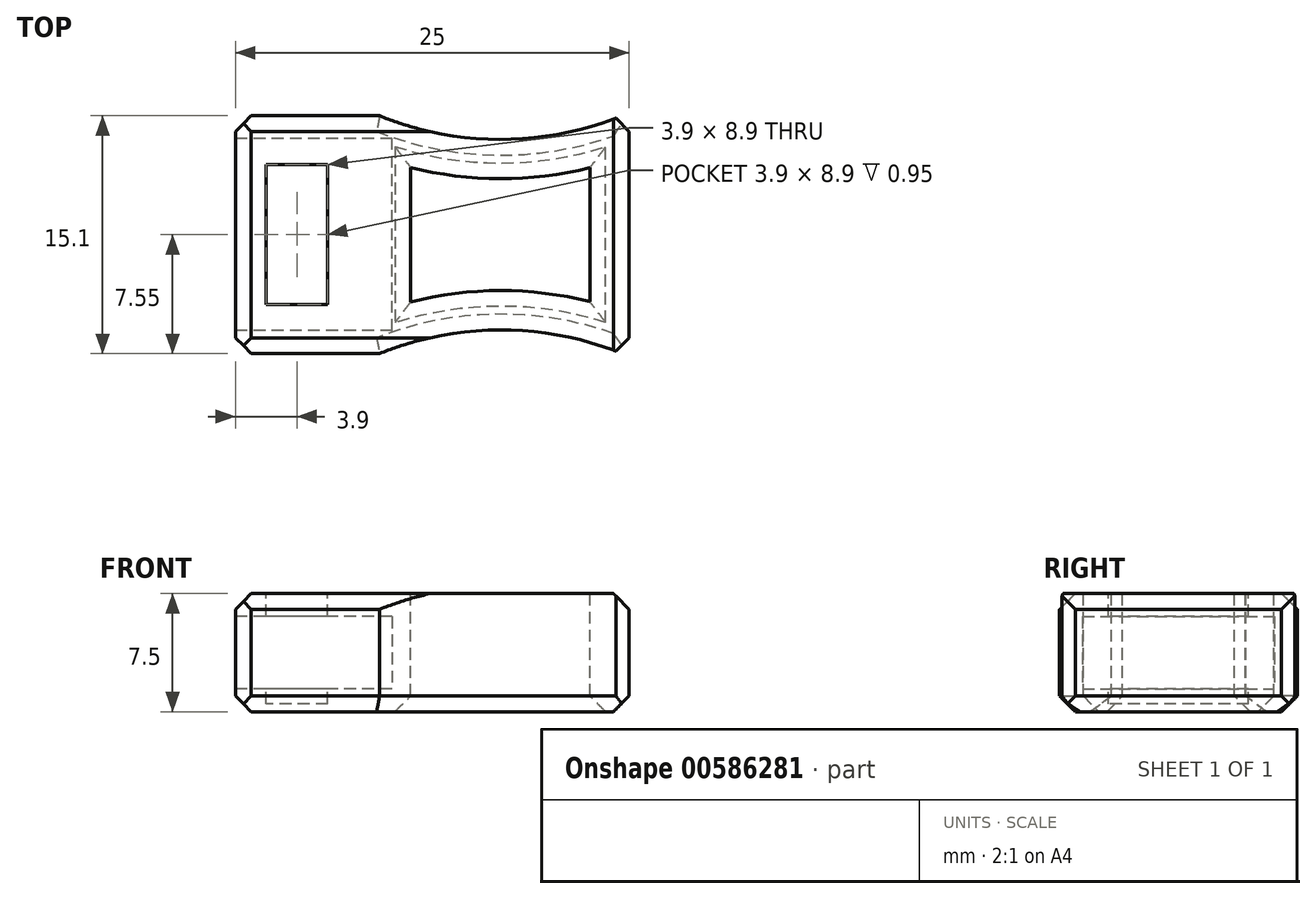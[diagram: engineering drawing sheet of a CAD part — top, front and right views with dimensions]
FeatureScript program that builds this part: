
annotation { "Feature Type Name" : "Feature", "Feature Type Description" : "" }
export const myFeature = defineFeature(function(context is Context, id is Id, definition is map)
    precondition{}
    {
        {
            var Q0;
            Q0=qCreatedBy(makeId("Top.planeOp"),FACE);
            var sketch = newSketch(context, id + "F0", { "sketchPlane" : qUnion([Q0])});
            skLineSegment(sketch, "E0.bottom", {"start": v(25, 7.55) * mm, "end": v(0, 7.55) * mm});
            skLineSegment(sketch, "E0.top", {"start": v(25, -7.55) * mm, "end": v(0, -7.55) * mm});
            skLineSegment(sketch, "E0.left", {"start": v(25, 7.55) * mm, "end": v(25, -7.55) * mm});
            skLineSegment(sketch, "E0.right", {"start": v(0, 7.55) * mm, "end": v(0, -7.55) * mm});
            skPoint(sketch, "E0.middle", {"position": v(0, 0) * mm});
            skSolve(sketch);
        }
        {
            var Q0;
            Q0 = qSketchRegion(id + "F0", true);
            extrude(context, id + "F1", {"entities" : qUnion([Q0]), "depth" : 7.5 * mm, "offsetDistance" : 25 * mm});
        }
        {
            var Q0;
            Q0=makeQuery(id+"F1.opExtrude","SWEPT_FACE",FACE,{"disambiguationData":[OSD([sQuery(id+"F0.wireOp",EDGE,"E0.right")])]});
            var sketch = newSketch(context, id + "F2", { "sketchPlane" : qUnion([Q0])});
            skLineSegment(sketch, "E1.bottom", {"start": v(6.1, 6.05) * mm, "end": v(-6.1, 6.05) * mm});
            skLineSegment(sketch, "E1.top", {"start": v(6.1, 1.45) * mm, "end": v(-6.1, 1.45) * mm});
            skLineSegment(sketch, "E1.left", {"start": v(6.1, 6.05) * mm, "end": v(6.1, 1.45) * mm});
            skLineSegment(sketch, "E1.right", {"start": v(-6.1, 6.05) * mm, "end": v(-6.1, 1.45) * mm});
            skPoint(sketch, "E1.middle", {"position": v(0, 3.75) * mm});
            skSolve(sketch);
        }
        {
            var Q0;
            Q0 = qSketchRegion(id + "F2", true);
            extrude(context, id + "F3", {"entities" : qUnion([Q0]), "operationType" : NewBodyOperationType.REMOVE, "oppositeDirection" : true, "depth" : 9.95 * mm, "offsetDistance" : 25 * mm});
        }
        {
            var Q0;
            Q0=makeQuery(id+"F1.opExtrude","CAP_FACE",FACE,{"disambiguationData":[OSD([sQuery(id+"F0.wireOp",EDGE,"E0.bottom"),sQuery(id+"F0.wireOp",EDGE,"E0.top"),sQuery(id+"F0.wireOp",EDGE,"E0.left"),sQuery(id+"F0.wireOp",EDGE,"E0.right")])],"isStart":false});
            var sketch = newSketch(context, id + "F4", { "sketchPlane" : qUnion([Q0])});
            skLineSegment(sketch, "E2.bottom", {"start": v(5.85, 4.45) * mm, "end": v(1.95, 4.45) * mm});
            skLineSegment(sketch, "E2.top", {"start": v(5.85, -4.45) * mm, "end": v(1.95, -4.45) * mm});
            skLineSegment(sketch, "E2.left", {"start": v(5.85, 4.45) * mm, "end": v(5.85, -4.45) * mm});
            skLineSegment(sketch, "E2.right", {"start": v(1.95, 4.45) * mm, "end": v(1.95, -4.45) * mm});
            skPoint(sketch, "E2.middle", {"position": v(3.9, 0) * mm});
            skSolve(sketch);
        }
        {
            var Q0;
            Q0 = qSketchRegion(id + "F4", true);
            extrude(context, id + "F5", {"entities" : qUnion([Q0]), "operationType" : NewBodyOperationType.REMOVE, "oppositeDirection" : true, "depth" : 25 * mm, "offsetDistance" : 25 * mm});
        }
        {
            var Q0;
            Q0=makeQuery(id+"F1.opExtrude","SWEPT_FACE",FACE,{"disambiguationData":[OSD([sQuery(id+"F0.wireOp",EDGE,"E0.left")])]});
            chamfer(context, id + "F6", {"entities" : qUnion([Q0]), "width" : 1 * mm, "tangentPropagation" : true});
        }
        {
            var Q0;
            Q0=makeQuery(id+"F1.opExtrude","CAP_EDGE",EDGE,{"disambiguationData":[OSD([sQuery(id+"F0.wireOp",EDGE,"E0.right")])],"isStart":false});
            var Q1;
            Q1=makeQuery(id+"F1.opExtrude","SWEPT_EDGE",EDGE,{"disambiguationData":[OSD([sQuery(id+"F0.wireOp",EDGE,"E0.top"),sQuery(id+"F0.wireOp",EDGE,"E0.right")])]});
            var Q2;
            Q2=makeQuery(id+"FrfRJ4BR4iio1pi_1.opChamfer","BLEND_EDGE",EDGE,{"blendedFrom":[makeQuery(id+"F1.opExtrude","CAP_EDGE",EDGE,{"disambiguationData":[OSD([sQuery(id+"F0.wireOp",EDGE,"E0.top")])],"isStart":false}),makeQuery(id+"F1.opExtrude","SWEPT_FACE",FACE,{"disambiguationData":[OSD([sQuery(id+"F0.wireOp",EDGE,"E0.right")])]})],"blendedInto":[makeQuery(id+"F1.opExtrude","SWEPT_FACE",FACE,{"disambiguationData":[OSD([sQuery(id+"F0.wireOp",EDGE,"E0.right")])]})]});
            var Q3;
            Q3=makeQuery(id+"FrfRJ4BR4iio1pi_1.opChamfer","BLEND_EDGE",EDGE,{"blendedFrom":[makeQuery(id+"F1.opExtrude","CAP_EDGE",EDGE,{"disambiguationData":[OSD([sQuery(id+"F0.wireOp",EDGE,"E0.top")])],"isStart":true}),makeQuery(id+"F1.opExtrude","SWEPT_FACE",FACE,{"disambiguationData":[OSD([sQuery(id+"F0.wireOp",EDGE,"E0.right")])]})],"blendedInto":[makeQuery(id+"F1.opExtrude","SWEPT_FACE",FACE,{"disambiguationData":[OSD([sQuery(id+"F0.wireOp",EDGE,"E0.right")])]})]});
            var Q4;
            Q4=makeQuery(id+"F1.opExtrude","CAP_EDGE",EDGE,{"disambiguationData":[OSD([sQuery(id+"F0.wireOp",EDGE,"E0.right")])],"isStart":true});
            var Q5;
            Q5=makeQuery(id+"FrfRJ4BR4iio1pi_1.opChamfer","BLEND_EDGE",EDGE,{"blendedFrom":[makeQuery(id+"F1.opExtrude","CAP_EDGE",EDGE,{"disambiguationData":[OSD([sQuery(id+"F0.wireOp",EDGE,"E0.bottom")])],"isStart":false}),makeQuery(id+"F1.opExtrude","SWEPT_FACE",FACE,{"disambiguationData":[OSD([sQuery(id+"F0.wireOp",EDGE,"E0.right")])]})],"blendedInto":[makeQuery(id+"F1.opExtrude","SWEPT_FACE",FACE,{"disambiguationData":[OSD([sQuery(id+"F0.wireOp",EDGE,"E0.right")])]})]});
            var Q6;
            Q6=makeQuery(id+"F1.opExtrude","SWEPT_EDGE",EDGE,{"disambiguationData":[OSD([sQuery(id+"F0.wireOp",EDGE,"E0.bottom"),sQuery(id+"F0.wireOp",EDGE,"E0.right")])]});
            var Q7;
            Q7=makeQuery(id+"FrfRJ4BR4iio1pi_1.opChamfer","BLEND_EDGE",EDGE,{"blendedFrom":[makeQuery(id+"F1.opExtrude","CAP_EDGE",EDGE,{"disambiguationData":[OSD([sQuery(id+"F0.wireOp",EDGE,"E0.bottom")])],"isStart":true}),makeQuery(id+"F1.opExtrude","SWEPT_FACE",FACE,{"disambiguationData":[OSD([sQuery(id+"F0.wireOp",EDGE,"E0.right")])]})],"blendedInto":[makeQuery(id+"F1.opExtrude","SWEPT_FACE",FACE,{"disambiguationData":[OSD([sQuery(id+"F0.wireOp",EDGE,"E0.right")])]})]});
            chamfer(context, id + "F7", {"entities" : qUnion([Q0, Q1, Q2, Q3, Q4, Q5, Q6, Q7]), "width" : 1 * mm, "tangentPropagation" : true});
        }
        {
            var Q0;
            Q0=makeQuery(id+"F1.opExtrude","CAP_FACE",FACE,{"disambiguationData":[OSD([sQuery(id+"F0.wireOp",EDGE,"E0.bottom"),sQuery(id+"F0.wireOp",EDGE,"E0.top"),sQuery(id+"F0.wireOp",EDGE,"E0.left"),sQuery(id+"F0.wireOp",EDGE,"E0.right")])],"isStart":false});
            var sketch = newSketch(context, id + "F8", { "sketchPlane" : qUnion([Q0])});
            skCircle(sketch, "E3", {"center": v(16.85, 26.55) * mm, "radius": 20.5 * mm});
            skCircle(sketch, "E4", {"center": v(16.85, -26.55) * mm, "radius": 20.5 * mm});
            skSolve(sketch);
        }
        {
            var Q0;
            Q0 = qSketchRegion(id + "F8", true);
            extrude(context, id + "F9", {"entities" : qUnion([Q0]), "operationType" : NewBodyOperationType.REMOVE, "oppositeDirection" : true, "depth" : 25 * mm, "offsetDistance" : 25 * mm});
        }
        {
            var Q0;
            Q0=makeQuery(id+"F9.boolean.opBoolean","COPY",EDGE,{"derivedFrom":makeQuery(id+"F9.opExtrude","CAP_EDGE",EDGE,{"disambiguationData":[OSD([sQuery(id+"F8.wireOp",EDGE,"E4")])],"isStart":true})});
            var Q1;
            Q1=makeQuery(id+"F1.opExtrude","CAP_EDGE",EDGE,{"disambiguationData":[OSD([sQuery(id+"F0.wireOp",EDGE,"E0.top")])],"isStart":false});
            var Q2;
            Q2=makeQuery(id+"F9.boolean.opBoolean","COPY",EDGE,{"derivedFrom":makeQuery(id+"F9.opExtrude","CAP_EDGE",EDGE,{"disambiguationData":[OSD([sQuery(id+"F8.wireOp",EDGE,"E3")])],"isStart":true})});
            var Q3;
            Q3=makeQuery(id+"F1.opExtrude","CAP_EDGE",EDGE,{"disambiguationData":[OSD([sQuery(id+"F0.wireOp",EDGE,"E0.bottom")])],"isStart":false});
            var Q4;
            Q4=makeQuery(id+"F9.boolean.opBoolean","INTERSECT",EDGE,{"derivedFrom":[makeQuery(id+"F1.opExtrude","CAP_FACE",FACE,{"disambiguationData":[OSD([sQuery(id+"F0.wireOp",EDGE,"E0.bottom"),sQuery(id+"F0.wireOp",EDGE,"E0.top"),sQuery(id+"F0.wireOp",EDGE,"E0.left"),sQuery(id+"F0.wireOp",EDGE,"E0.right")])],"isStart":true}),makeQuery(id+"F9.opExtrude","SWEPT_FACE",FACE,{"disambiguationData":[OSD([sQuery(id+"F8.wireOp",EDGE,"E4")])]})]});
            var Q5;
            Q5=makeQuery(id+"F1.opExtrude","CAP_EDGE",EDGE,{"disambiguationData":[OSD([sQuery(id+"F0.wireOp",EDGE,"E0.top")])],"isStart":true});
            var Q6;
            Q6=makeQuery(id+"F9.boolean.opBoolean","INTERSECT",EDGE,{"derivedFrom":[makeQuery(id+"F1.opExtrude","CAP_FACE",FACE,{"disambiguationData":[OSD([sQuery(id+"F0.wireOp",EDGE,"E0.bottom"),sQuery(id+"F0.wireOp",EDGE,"E0.top"),sQuery(id+"F0.wireOp",EDGE,"E0.left"),sQuery(id+"F0.wireOp",EDGE,"E0.right")])],"isStart":true}),makeQuery(id+"F9.opExtrude","SWEPT_FACE",FACE,{"disambiguationData":[OSD([sQuery(id+"F8.wireOp",EDGE,"E3")])]})]});
            var Q7;
            Q7=makeQuery(id+"F1.opExtrude","CAP_EDGE",EDGE,{"disambiguationData":[OSD([sQuery(id+"F0.wireOp",EDGE,"E0.bottom")])],"isStart":true});
            chamfer(context, id + "F10", {"entities" : qUnion([Q0, Q1, Q2, Q3, Q4, Q5, Q6, Q7]), "width" : 1 * mm, "tangentPropagation" : true});
        }
        {
            var Q0;
            Q0=makeQuery(id+"F1.opExtrude","CAP_FACE",FACE,{"disambiguationData":[OSD([sQuery(id+"F0.wireOp",EDGE,"E0.bottom"),sQuery(id+"F0.wireOp",EDGE,"E0.top"),sQuery(id+"F0.wireOp",EDGE,"E0.left"),sQuery(id+"F0.wireOp",EDGE,"E0.right")])],"isStart":false});
            var sketch = newSketch(context, id + "F11", { "sketchPlane" : qUnion([Q0])});
            skLineSegment(sketch, "E5.0", {"start": v(22.5, -4.25) * mm, "end": v(22.5, 4.25) * mm});
            skArc(sketch, "E5.3", {"start": v(22.5, 4.25) * mm, "mid": v(16.8, 3.55) * mm, "end": v(11.12, 4.28) * mm});
            skArc(sketch, "E5.5", {"start": v(11.12, -4.28) * mm, "mid": v(16.8, -3.55) * mm, "end": v(22.5, -4.25) * mm});
            skLineSegment(sketch, "E6", {"start": v(11.12, -4.28) * mm, "end": v(11.12, 4.28) * mm});
            skSolve(sketch);
        }
        {
            var Q0;
            Q0 = qSketchRegion(id + "F11", true);
            extrude(context, id + "F12", {"entities" : qUnion([Q0]), "operationType" : NewBodyOperationType.REMOVE, "oppositeDirection" : true, "depth" : 25 * mm, "offsetDistance" : 25 * mm});
        }
        {
            var Q0;
            Q0=makeQuery(id+"F12.boolean.opBoolean","COPY",EDGE,{"derivedFrom":makeQuery(id+"F12.opExtrude","CAP_EDGE",EDGE,{"disambiguationData":[OSD([sQuery(id+"F11.wireOp",EDGE,"E6")])],"isStart":true})});
            var Q1;
            Q1=makeQuery(id+"F12.boolean.opBoolean","COPY",EDGE,{"derivedFrom":makeQuery(id+"F12.opExtrude","CAP_EDGE",EDGE,{"disambiguationData":[OSD([sQuery(id+"F11.wireOp",EDGE,"E5.3")])],"isStart":true})});
            var Q2;
            Q2=makeQuery(id+"F12.boolean.opBoolean","COPY",EDGE,{"derivedFrom":makeQuery(id+"F12.opExtrude","CAP_EDGE",EDGE,{"disambiguationData":[OSD([sQuery(id+"F11.wireOp",EDGE,"E5.0")])],"isStart":true})});
            var Q3;
            Q3=makeQuery(id+"F12.boolean.opBoolean","COPY",EDGE,{"derivedFrom":makeQuery(id+"F12.opExtrude","CAP_EDGE",EDGE,{"disambiguationData":[OSD([sQuery(id+"F11.wireOp",EDGE,"E5.5")])],"isStart":true})});
            var Q4;
            Q4=makeQuery(id+"F12.boolean.opBoolean","INTERSECT",EDGE,{"derivedFrom":[makeQuery(id+"F1.opExtrude","CAP_FACE",FACE,{"disambiguationData":[OSD([sQuery(id+"F0.wireOp",EDGE,"E0.bottom"),sQuery(id+"F0.wireOp",EDGE,"E0.top"),sQuery(id+"F0.wireOp",EDGE,"E0.left"),sQuery(id+"F0.wireOp",EDGE,"E0.right")])],"isStart":true}),makeQuery(id+"F12.opExtrude","SWEPT_FACE",FACE,{"disambiguationData":[OSD([sQuery(id+"F11.wireOp",EDGE,"E6")])]})]});
            var Q5;
            Q5=makeQuery(id+"F12.boolean.opBoolean","INTERSECT",EDGE,{"derivedFrom":[makeQuery(id+"F1.opExtrude","CAP_FACE",FACE,{"disambiguationData":[OSD([sQuery(id+"F0.wireOp",EDGE,"E0.bottom"),sQuery(id+"F0.wireOp",EDGE,"E0.top"),sQuery(id+"F0.wireOp",EDGE,"E0.left"),sQuery(id+"F0.wireOp",EDGE,"E0.right")])],"isStart":true}),makeQuery(id+"F12.opExtrude","SWEPT_FACE",FACE,{"disambiguationData":[OSD([sQuery(id+"F11.wireOp",EDGE,"E5.3")])]})]});
            var Q6;
            Q6=makeQuery(id+"F12.boolean.opBoolean","INTERSECT",EDGE,{"derivedFrom":[makeQuery(id+"F1.opExtrude","CAP_FACE",FACE,{"disambiguationData":[OSD([sQuery(id+"F0.wireOp",EDGE,"E0.bottom"),sQuery(id+"F0.wireOp",EDGE,"E0.top"),sQuery(id+"F0.wireOp",EDGE,"E0.left"),sQuery(id+"F0.wireOp",EDGE,"E0.right")])],"isStart":true}),makeQuery(id+"F12.opExtrude","SWEPT_FACE",FACE,{"disambiguationData":[OSD([sQuery(id+"F11.wireOp",EDGE,"E5.0")])]})]});
            var Q7;
            Q7=makeQuery(id+"F12.boolean.opBoolean","INTERSECT",EDGE,{"derivedFrom":[makeQuery(id+"F1.opExtrude","CAP_FACE",FACE,{"disambiguationData":[OSD([sQuery(id+"F0.wireOp",EDGE,"E0.bottom"),sQuery(id+"F0.wireOp",EDGE,"E0.top"),sQuery(id+"F0.wireOp",EDGE,"E0.left"),sQuery(id+"F0.wireOp",EDGE,"E0.right")])],"isStart":true}),makeQuery(id+"F12.opExtrude","SWEPT_FACE",FACE,{"disambiguationData":[OSD([sQuery(id+"F11.wireOp",EDGE,"E5.5")])]})]});
            chamfer(context, id + "F13", {"entities" : qUnion([Q0, Q1, Q2, Q3, Q4, Q5, Q6, Q7]), "width" : 1 * mm, "tangentPropagation" : true});
        }
        {
            var Q0;
            Q0=makeQuery(id+"F1.opExtrude","CAP_FACE",FACE,{"disambiguationData":[OSD([sQuery(id+"F0.wireOp",EDGE,"E0.bottom"),sQuery(id+"F0.wireOp",EDGE,"E0.top"),sQuery(id+"F0.wireOp",EDGE,"E0.left"),sQuery(id+"F0.wireOp",EDGE,"E0.right")])],"isStart":true});
            var sketch = newSketch(context, id + "F14", { "sketchPlane" : qUnion([Q0])});
            skLineSegment(sketch, "E7.bottom", {"start": v(1.46, 4.94) * mm, "end": v(8.37, 4.94) * mm});
            skLineSegment(sketch, "E7.top", {"start": v(1.46, -5) * mm, "end": v(8.37, -5) * mm});
            skLineSegment(sketch, "E7.left", {"start": v(1.46, 4.94) * mm, "end": v(1.46, -5) * mm});
            skLineSegment(sketch, "E7.right", {"start": v(8.37, 4.94) * mm, "end": v(8.37, -5) * mm});
            skSolve(sketch);
        }
        {
            var Q0;
            Q0 = qSketchRegion(id + "F14", true);
            extrude(context, id + "F15", {"entities" : qUnion([Q0]), "operationType" : NewBodyOperationType.ADD, "oppositeDirection" : true, "depth" : .5 * mm, "offsetDistance" : 25 * mm});
        }
    });
